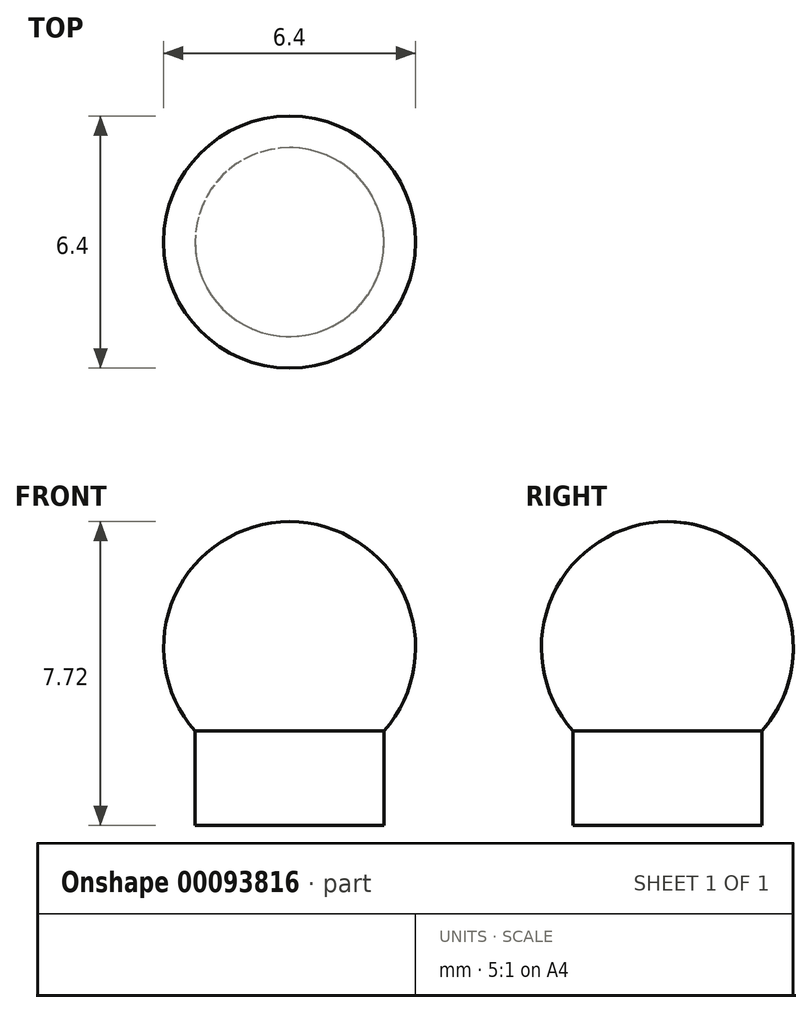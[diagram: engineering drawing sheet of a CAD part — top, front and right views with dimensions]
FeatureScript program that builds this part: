
annotation { "Feature Type Name" : "Feature", "Feature Type Description" : "" }
export const myFeature = defineFeature(function(context is Context, id is Id, definition is map)
    precondition{}
    {
        {
            var Q0;
            Q0=qCreatedBy(makeId("Right.planeOp"),FACE);
            var sketch = newSketch(context, id + "F0", { "sketchPlane" : qUnion([Q0])});
            skLineSegment(sketch, "E0.bottom", {"start": v(0, 0) * mm, "end": v(2.4, 0) * mm});
            skLineSegment(sketch, "E0.right", {"start": v(2.4, 0) * mm, "end": v(2.4, 2.4) * mm});
            skArc(sketch, "E1", {"start": v(2.4, 2.4) * mm, "mid": v(2.92, 5.83) * mm, "end": v(0, 7.72) * mm});
            skLineSegment(sketch, "E2", {"start": v(0, 0) * mm, "end": v(0, 7.72) * mm});
            skArc(sketch, "E3.MirrorCS", {"start": v(-2.4, 2.4) * mm, "mid": v(-2.92, 5.83) * mm, "end": v(0, 7.72) * mm, "construction": true});
            skLineSegment(sketch, "E4.MirrorCS", {"start": v(-2.4, 0) * mm, "end": v(-2.4, 2.4) * mm, "construction": true});
            skLineSegment(sketch, "E5.MirrorCS", {"start": v(0, 0) * mm, "end": v(-2.4, 0) * mm, "construction": true});
            skSolve(sketch);
        }
        {
            var Q0;
            Q0=makeQuery(id+"F0.imprint","IMPRINT",FACE,{"disambiguationData":[TD([[makeQuery(id+"F0.imprint","IMPRINT",EDGE,{"derivedFrom":sQuery(id+"F0.wireOp",EDGE,"E0.bottom")}),1.0]])]});
            var Q1;
            Q1=sQuery(id+"F0.wireOp",EDGE,"E2");
            revolve(context, id + "F1", {"entities" : qUnion([Q0]), "axis" : qUnion([Q1]), "revolveType" : RevolveType.FULL});
        }
    });
